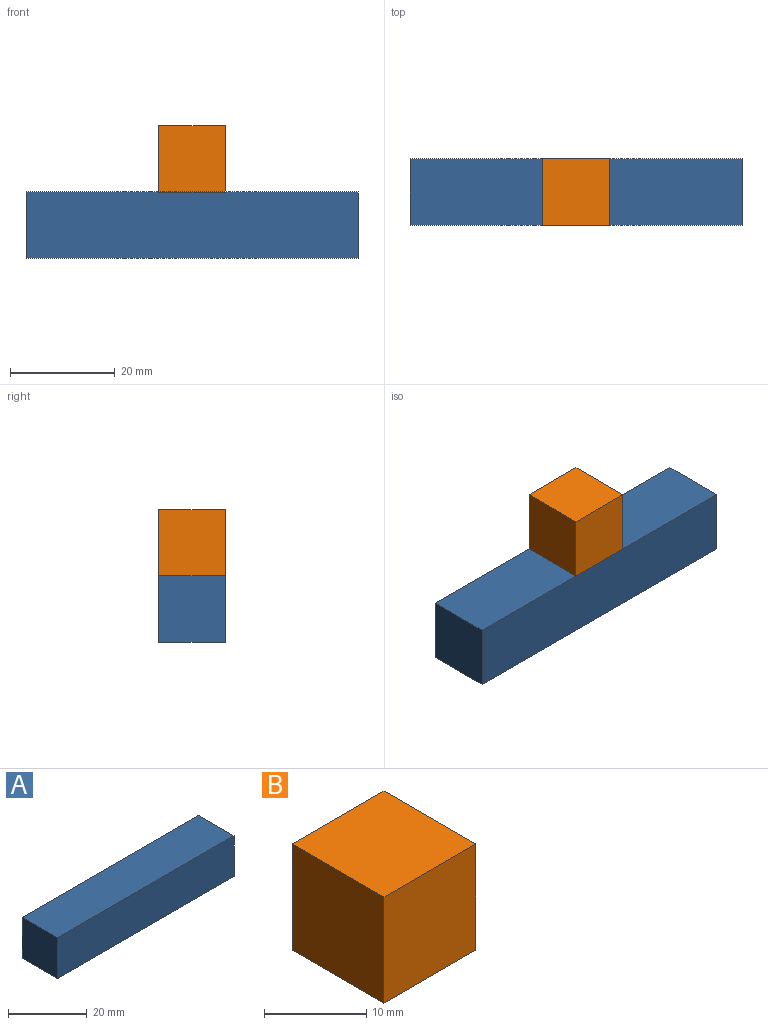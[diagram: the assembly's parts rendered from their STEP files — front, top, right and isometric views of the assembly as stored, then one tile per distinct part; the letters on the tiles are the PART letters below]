
ASSEMBLY  parts=2 mates=1
PART A: 6 faces, bbox 63.5x12.7x12.7 mm
  f0: plane 63.5x12.7mm, normal (0,0,-1), area 806.5mm2, adj f1,f3,f4,f5
  f1: plane 12.7x12.7mm, normal (1,0,0), area 161.3mm2, adj f0,f2,f4,f5
  f2: plane 63.5x12.7mm, normal (0,0,1), area 806.5mm2, adj f1,f3,f4,f5
  f3: plane 12.7x12.7mm, normal (-1,0,0), area 161.3mm2, adj f0,f2,f4,f5
  f4: plane 63.5x12.7mm, normal (0,-1,0), area 806.5mm2, adj f0,f1,f2,f3
  f5: plane 63.5x12.7mm, normal (0,1,0), area 806.5mm2, adj f0,f1,f2,f3
PART B: 6 faces, bbox 12.7x12.7x12.7 mm
  f0: plane 12.7x12.7mm, normal (0,0,-1), area 161.3mm2, adj f1,f3,f4,f5
  f1: plane 12.7x12.7mm, normal (1,0,0), area 161.3mm2, adj f0,f2,f4,f5
  f2: plane 12.7x12.7mm, normal (0,0,1), area 161.3mm2, adj f1,f3,f4,f5
  f3: plane 12.7x12.7mm, normal (-1,0,0), area 161.3mm2, adj f0,f2,f4,f5
  f4: plane 12.7x12.7mm, normal (0,-1,0), area 161.3mm2, adj f0,f1,f2,f3
  f5: plane 12.7x12.7mm, normal (0,1,0), area 161.3mm2, adj f0,f1,f2,f3
PLACE A t=(-20.27,-10.38,31.05)mm
PLACE B t=(-23.58,-10.38,-28.43)mm
MATE planar A.f2 <-> B.f0  axis (0,0,1) through (-23.58,-16.73,-6.21)mm
